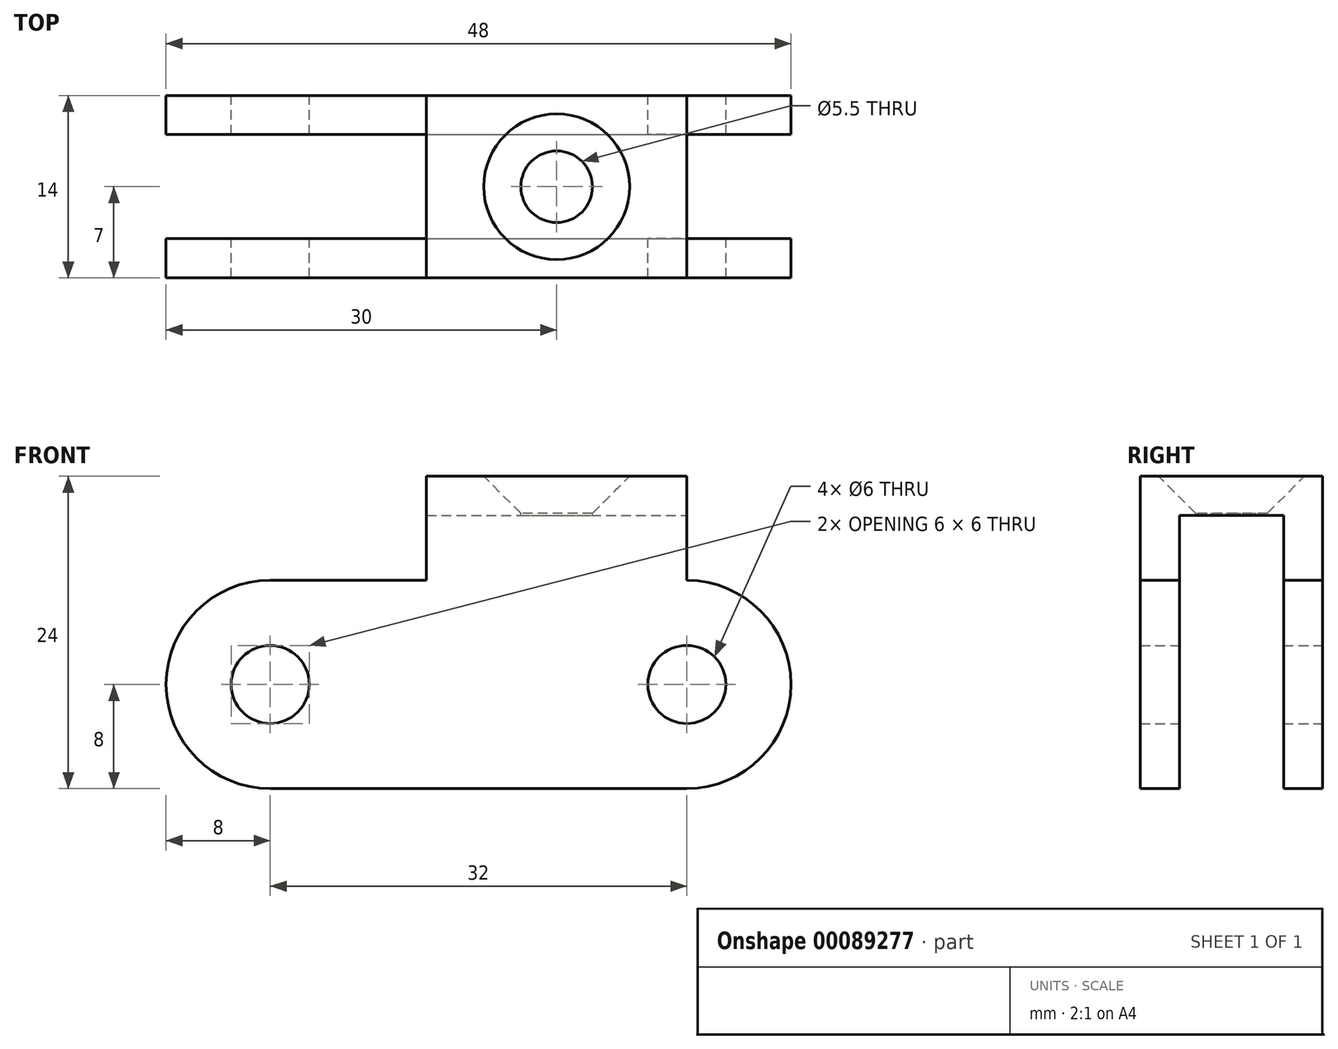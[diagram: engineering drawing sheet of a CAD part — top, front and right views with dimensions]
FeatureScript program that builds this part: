
annotation { "Feature Type Name" : "Feature", "Feature Type Description" : "" }
export const myFeature = defineFeature(function(context is Context, id is Id, definition is map)
    precondition{}
    {
        {
            var Q0;
            Q0=qCreatedBy(makeId("Front.planeOp"),FACE);
            var sketch = newSketch(context, id + "F0", { "sketchPlane" : qUnion([Q0])});
            skLineSegment(sketch, "E0.bottom", {"start": v(0, 0) * mm, "end": v(48, 0) * mm});
            skLineSegment(sketch, "E0.top", {"start": v(0, 16) * mm, "end": v(48, 16) * mm});
            skLineSegment(sketch, "E0.left", {"start": v(0, 0) * mm, "end": v(0, 16) * mm});
            skLineSegment(sketch, "E0.right", {"start": v(48, 0) * mm, "end": v(48, 16) * mm});
            skLineSegment(sketch, "E1.bottom", {"start": v(20, 16) * mm, "end": v(40, 16) * mm});
            skLineSegment(sketch, "E1.top", {"start": v(20, 24) * mm, "end": v(40, 24) * mm});
            skLineSegment(sketch, "E1.left", {"start": v(20, 16) * mm, "end": v(20, 24) * mm});
            skLineSegment(sketch, "E1.right", {"start": v(40, 16) * mm, "end": v(40, 24) * mm});
            skCircle(sketch, "E2", {"center": v(8, 8) * mm, "radius": 3 * mm});
            skCircle(sketch, "E3", {"center": v(40, 8) * mm, "radius": 3 * mm});
            skLineSegment(sketch, "E4", {"start": v(48, 8) * mm, "end": v(0, 8) * mm, "construction": true});
            skSolve(sketch);
        }
        {
            var Q0;
            Q0 = qSketchRegion(id + "F0", true);
            extrude(context, id + "F1", {"entities" : qUnion([Q0]), "depth" : 14 * mm});
        }
        {
            var Q0;
            Q0=makeQuery(id+"F1.opExtrude","SWEPT_EDGE",EDGE,{"disambiguationData":[OSD([sQuery(id+"F0.wireOp",EDGE,"E0.top"),sQuery(id+"F0.wireOp",EDGE,"E0.left")])]});
            var Q1;
            Q1=makeQuery(id+"F1.opExtrude","SWEPT_EDGE",EDGE,{"disambiguationData":[OSD([sQuery(id+"F0.wireOp",EDGE,"E0.bottom"),sQuery(id+"F0.wireOp",EDGE,"E0.left")])]});
            var Q2;
            Q2=makeQuery(id+"F1.opExtrude","SWEPT_EDGE",EDGE,{"disambiguationData":[OSD([sQuery(id+"F0.wireOp",EDGE,"E0.top"),sQuery(id+"F0.wireOp",EDGE,"E0.right")])]});
            var Q3;
            Q3=makeQuery(id+"F1.opExtrude","SWEPT_EDGE",EDGE,{"disambiguationData":[OSD([sQuery(id+"F0.wireOp",EDGE,"E0.bottom"),sQuery(id+"F0.wireOp",EDGE,"E0.right")])]});
            fillet(context, id + "F2", {"entities" : qUnion([Q0, Q1, Q2, Q3]), "radius" : 8 * mm, "tangentPropagation" : true, "allowEdgeOverflow" : false});
        }
        {
            var Q0;
            Q0=makeQuery(id+"F1.opExtrude","SWEPT_FACE",FACE,{"disambiguationData":[OSD([sQuery(id+"F0.wireOp",EDGE,"E0.bottom")])]});
            var sketch = newSketch(context, id + "F3", { "sketchPlane" : qUnion([Q0])});
            skLineSegment(sketch, "E5.bottom", {"start": v(-1.37, 3) * mm, "end": v(61.6, 3) * mm});
            skLineSegment(sketch, "E5.top", {"start": v(-1.37, 11) * mm, "end": v(61.6, 11) * mm});
            skLineSegment(sketch, "E5.left", {"start": v(-1.37, 3) * mm, "end": v(-1.37, 11) * mm});
            skLineSegment(sketch, "E5.right", {"start": v(61.6, 3) * mm, "end": v(61.6, 11) * mm});
            skSolve(sketch);
        }
        {
            var Q0;
            Q0 = qSketchRegion(id + "F3", true);
            extrude(context, id + "F4", {"entities" : qUnion([Q0]), "operationType" : NewBodyOperationType.REMOVE, "oppositeDirection" : true, "depth" : 21 * mm});
        }
        {
            var Q0;
            Q0=makeQuery(id+"F1.opExtrude","SWEPT_FACE",FACE,{"disambiguationData":[OSD([sQuery(id+"F0.wireOp",EDGE,"E1.top")])]});
            var sketch = newSketch(context, id + "F5", { "sketchPlane" : qUnion([Q0])});
            skPoint(sketch, "E6", {"position": v(30, -7) * mm});
            skPoint(sketch, "E6.positionSnap0", {"position": v(20, -7) * mm});
            skPoint(sketch, "E6.positionSnap1", {"position": v(30, 0) * mm});
            skSolve(sketch);
        }
        {
            var Q0;
            Q0=sQuery(id+"F5.wireOp",VERTEX,"E6");
            var Q1;
            Q1=makeQuery(id+"F1.opExtrude","SWEPT_BODY",BODY,{"disambiguationData":[OSD([sQuery(id+"F0.wireOp",EDGE,"E0.bottom"),sQuery(id+"F0.wireOp",EDGE,"E0.top"),sQuery(id+"F0.wireOp",EDGE,"E0.left"),sQuery(id+"F0.wireOp",EDGE,"E0.right"),sQuery(id+"F0.wireOp",EDGE,"E1.top"),sQuery(id+"F0.wireOp",EDGE,"E1.left"),sQuery(id+"F0.wireOp",EDGE,"E1.right"),sQuery(id+"F0.wireOp",EDGE,"E2"),sQuery(id+"F0.wireOp",EDGE,"E3")])]});
            hole(context, id + "F6", {"style" : HoleStyle.C_SINK, "endStyle" : HoleEndStyle.THROUGH, "standardTappedOrClearance" : lookupTablePath({ "standard" : "ISO", "fit" : "Normal", "size" : "M5", "type" : "Clearance" }), "standardBlindInLast" : lookupTablePath({ "fit" : "Standard", "standard" : "ISO", "size" : "M5", "type" : "Clearance" }), "holeDiameter" : 5.5 * mm, "cSinkDiameter" : 11.2 * mm, "cSinkAngle" : 90 * degree, "locations" : qUnion([Q0]), "scope" : qUnion([Q1]), "isTappedThrough" : true});
        }
    });
